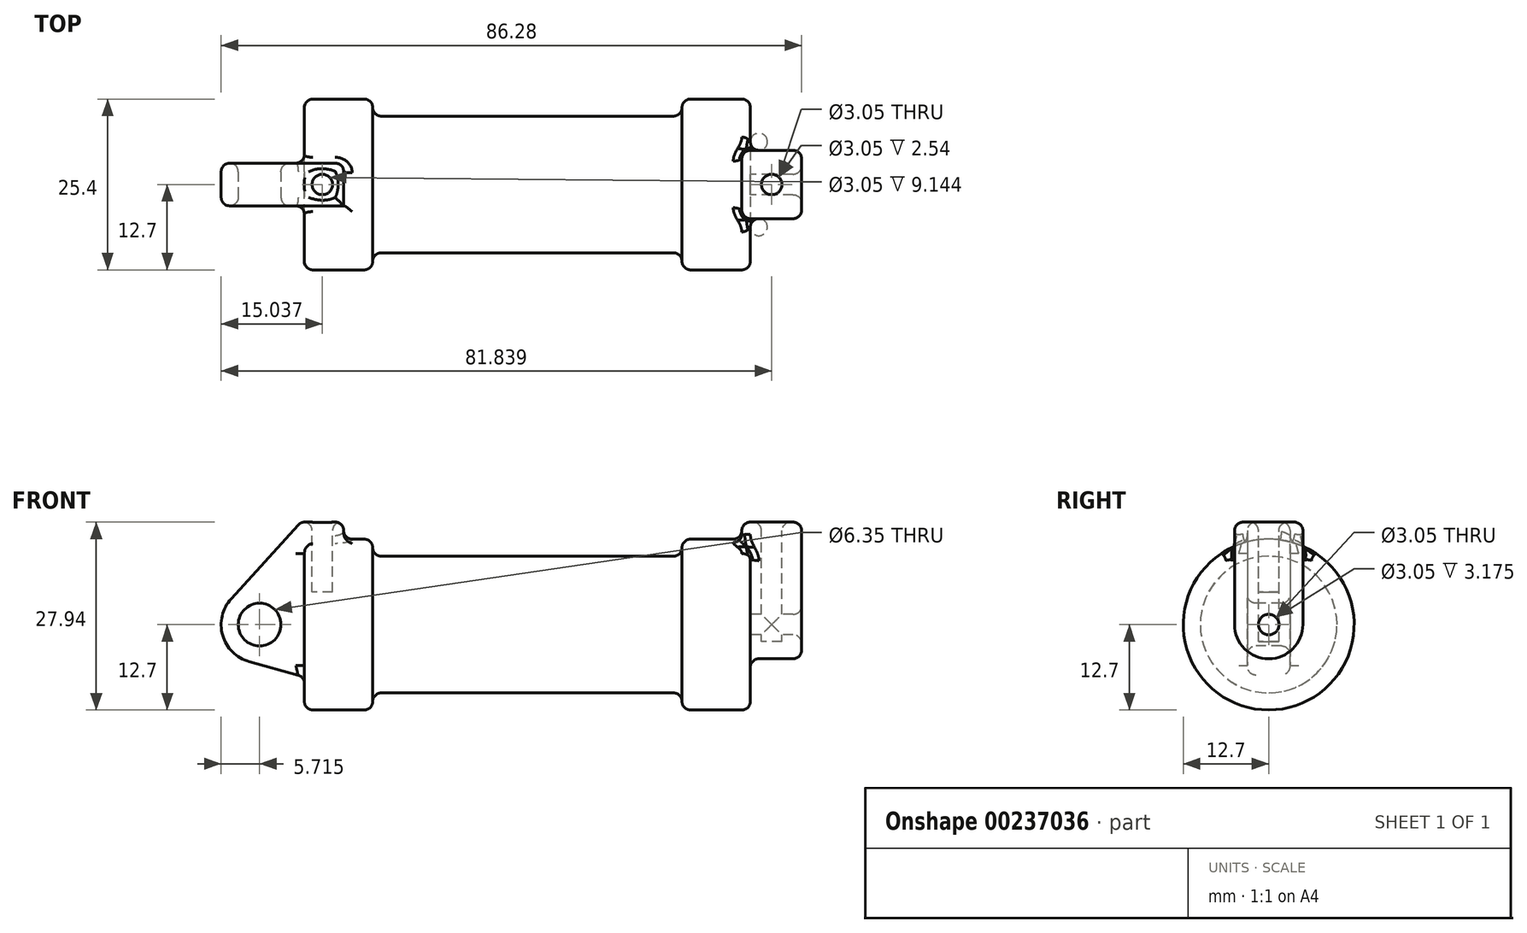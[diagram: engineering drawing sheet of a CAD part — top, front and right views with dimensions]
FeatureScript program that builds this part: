
annotation { "Feature Type Name" : "Feature", "Feature Type Description" : "" }
export const myFeature = defineFeature(function(context is Context, id is Id, definition is map)
    precondition{}
    {
        {
            var Q0;
            Q0=qCreatedBy(makeId("Front.planeOp"),FACE);
            var sketch = newSketch(context, id + "F0", { "sketchPlane" : qUnion([Q0])});
            skLineSegment(sketch, "E0", {"start": v(0, 0) * mm, "end": v(0, 12.7) * mm});
            skLineSegment(sketch, "E1", {"start": v(0, 12.7) * mm, "end": v(10.16, 12.7) * mm});
            skLineSegment(sketch, "E2", {"start": v(10.16, 12.7) * mm, "end": v(10.16, 10.16) * mm});
            skLineSegment(sketch, "E3", {"start": v(10.16, 10.16) * mm, "end": v(56.13, 10.16) * mm});
            skLineSegment(sketch, "E4", {"start": v(56.13, 10.16) * mm, "end": v(56.13, 12.7) * mm});
            skLineSegment(sketch, "E5", {"start": v(56.13, 12.7) * mm, "end": v(66.3, 12.7) * mm});
            skLineSegment(sketch, "E6", {"start": v(66.3, 12.7) * mm, "end": v(66.3, 0) * mm});
            skLineSegment(sketch, "E7", {"start": v(66.3, 0) * mm, "end": v(0, 0) * mm});
            skLineSegment(sketch, "E8", {"start": v(5.84, 15.24) * mm, "end": v(-0.5, 15.24) * mm});
            skLineSegment(sketch, "E9", {"start": v(-0.5, 15.24) * mm, "end": v(-10.88, 3.85) * mm});
            skLineSegment(sketch, "E10", {"start": v(0, 0) * mm, "end": v(-6.65, 0) * mm});
            skCircle(sketch, "E11", {"center": v(-6.65, 0) * mm, "radius": 5.72 * mm});
            skCircle(sketch, "E12", {"center": v(-6.65, 0) * mm, "radius": 3.18 * mm});
            skLineSegment(sketch, "E13", {"start": v(5.84, 15.24) * mm, "end": v(5.84, -9.4) * mm});
            skLineSegment(sketch, "E14", {"start": v(5.84, -9.4) * mm, "end": v(-8.18, -5.5) * mm});
            skSolve(sketch);
        }
        {
            var Q0;
            {var subQ0=sQuery(id+"F0.wireOp",EDGE,"E2");Q0=makeQuery(id+"F0.imprint","IMPRINT",FACE,{"disambiguationData":[TD([[makeQuery(id+"F0.imprint","IMPRINT",EDGE,{"derivedFrom":subQ0}),-1.0]])]});}
            var Q1;
            {var subQ0=sQuery(id+"F0.wireOp",EDGE,"E0");Q1=makeQuery(id+"F0.imprint","IMPRINT",FACE,{"disambiguationData":[TD([[makeQuery(id+"F0.imprint","IMPRINT",EDGE,{"derivedFrom":subQ0}),-1.0]])]});}
            var Q2;
            Q2=sQuery(id+"F0.wireOp",EDGE,"E7");
            revolve(context, id + "F1", {"entities" : qUnion([Q0, Q1]), "axis" : qUnion([Q2]), "revolveType" : RevolveType.FULL});
        }
        {
            var Q0;
            {var subQ0=sQuery(id+"F0.wireOp",EDGE,"E0");Q0=makeQuery(id+"F0.imprint","IMPRINT",FACE,{"disambiguationData":[TD([[makeQuery(id+"F0.imprint","IMPRINT",EDGE,{"derivedFrom":subQ0}),-1.0]])]});}
            var Q1;
            {var subQ3=sQuery(id+"F0.wireOp",EDGE,"E0");Q1=makeQuery(id+"F0.imprint","IMPRINT",FACE,{"disambiguationData":[TD([[makeQuery(id+"F0.imprint","IMPRINT",EDGE,{"derivedFrom":subQ3}),1.0]])]});}
            var Q2;
            {var subQ0=sQuery(id+"F0.wireOp",EDGE,"E14");Q2=makeQuery(id+"F0.imprint","IMPRINT",FACE,{"disambiguationData":[TD([[makeQuery(id+"F0.imprint","IMPRINT",EDGE,{"derivedFrom":subQ0}),-1.0]])]});}
            var Q3;
            {var subQ4=sQuery(id+"F0.wireOp",EDGE,"E12");Q3=makeQuery(id+"F0.imprint","IMPRINT",FACE,{"disambiguationData":[TD([[makeQuery(id+"F0.imprint","IMPRINT",EDGE,{"derivedFrom":subQ4}),-1.0]])]});}
            extrude(context, id + "F2", {"entities" : qUnion([Q0, Q1, Q2, Q3]), "operationType" : NewBodyOperationType.ADD, "endBound" : BoundingType.SYMMETRIC, "oppositeDirection" : true, "depth" : 6.35 * mm});
        }
        {
            var Q0;
            Q0=makeQuery(id+"F1.opRevolve","SWEPT_FACE",FACE,{"disambiguationData":[OSD([sQuery(id+"F0.wireOp",EDGE,"E6")])]});
            var sketch = newSketch(context, id + "F3", { "sketchPlane" : qUnion([Q0])});
            skCircle(sketch, "E15", {"center": v(0, 0) * mm, "radius": 1.52 * mm});
            skCircle(sketch, "E16", {"center": v(0, 0) * mm, "radius": 5.08 * mm});
            skLineSegment(sketch, "E17", {"start": v(-5.08, 0) * mm, "end": v(-5.08, 15.24) * mm});
            skLineSegment(sketch, "E18", {"start": v(-5.08, 15.24) * mm, "end": v(5.08, 15.24) * mm});
            skLineSegment(sketch, "E19", {"start": v(5.08, 15.24) * mm, "end": v(5.08, 0) * mm});
            skSolve(sketch);
        }
        {
            var Q0;
            Q0 = qSketchRegion(id + "F3", true);
            extrude(context, id + "F4", {"entities" : qUnion([Q0]), "operationType" : NewBodyOperationType.ADD, "depth" : 7.62 * mm, "hasSecondDirection" : true, "secondDirectionOppositeDirection" : true, "secondDirectionDepth" : 1.27 * mm});
        }
        {
            var Q0;
            Q0=makeQuery(id+"F4.opExtrude","SWEPT_FACE",FACE,{"disambiguationData":[OSD([sQuery(id+"F3.wireOp",EDGE,"E18")])]});
            var sketch = newSketch(context, id + "F5", { "sketchPlane" : qUnion([Q0])});
            skCircle(sketch, "E20", {"center": v(69.47, 0) * mm, "radius": 1.52 * mm});
            skSolve(sketch);
        }
        {
            var Q0;
            Q0=makeQuery(id+"F2.opExtrude","SWEPT_FACE",FACE,{"disambiguationData":[OSD([sQuery(id+"F0.wireOp",EDGE,"E8")])]});
            var sketch = newSketch(context, id + "F6", { "sketchPlane" : qUnion([Q0])});
            skCircle(sketch, "E21", {"center": v(2.67, 0) * mm, "radius": 1.52 * mm});
            skSolve(sketch);
        }
        {
            var Q0;
            Q0 = qSketchRegion(id + "F5", true);
            extrude(context, id + "F7", {"entities" : qUnion([Q0]), "operationType" : NewBodyOperationType.REMOVE, "oppositeDirection" : true, "depth" : 17.78 * mm});
        }
        {
            var Q0;
            Q0 = qSketchRegion(id + "F6", true);
            extrude(context, id + "F8", {"entities" : qUnion([Q0]), "operationType" : NewBodyOperationType.REMOVE, "oppositeDirection" : true, "depth" : 10.4 * mm});
        }
        {
            var Q0;
            Q0=makeQuery(id+"F1.opRevolve","SWEPT_FACE",FACE,{"disambiguationData":[OSD([sQuery(id+"F0.wireOp",EDGE,"E5")])]});
            var Q1;
            Q1=makeQuery(id+"F1.opRevolve","SWEPT_FACE",FACE,{"disambiguationData":[OSD([sQuery(id+"F0.wireOp",EDGE,"E3")])]});
            var Q2;
            Q2=makeQuery(id+"F4.opExtrude","SWEPT_FACE",FACE,{"disambiguationData":[OSD([sQuery(id+"F3.wireOp",EDGE,"E19")])]});
            var Q3;
            Q3=makeQuery(id+"F4.opExtrude","CAP_FACE",FACE,{"disambiguationData":[OSD([sQuery(id+"F3.wireOp",EDGE,"E15"),sQuery(id+"F3.wireOp",EDGE,"E16"),sQuery(id+"F3.wireOp",EDGE,"E17"),sQuery(id+"F3.wireOp",EDGE,"E18"),sQuery(id+"F3.wireOp",EDGE,"E19")])],"isStart":true});
            var Q4;
            Q4=makeQuery(id+"F4.opExtrude","SWEPT_FACE",FACE,{"disambiguationData":[OSD([sQuery(id+"F3.wireOp",EDGE,"E18")])]});
            var Q5;
            Q5=makeQuery(id+"F1.opRevolve","SWEPT_EDGE",EDGE,{"disambiguationData":[OSD([sQuery(id+"F0.wireOp",EDGE,"E4"),sQuery(id+"F0.wireOp",EDGE,"E5")])]});
            var Q6;
            Q6=makeQuery(id+"F1.opRevolve","SWEPT_EDGE",EDGE,{"disambiguationData":[OSD([sQuery(id+"F0.wireOp",EDGE,"E0"),sQuery(id+"F0.wireOp",EDGE,"E1")])]});
            var Q7;
            Q7=makeQuery(id+"F1.opRevolve","SWEPT_FACE",FACE,{"disambiguationData":[OSD([sQuery(id+"F0.wireOp",EDGE,"E1")])]});
            var Q8;
            Q8=makeQuery(id+"F2.opExtrude","CAP_FACE",FACE,{"disambiguationData":[OSD([sQuery(id+"F0.wireOp",EDGE,"E8"),sQuery(id+"F0.wireOp",EDGE,"E9"),sQuery(id+"F0.wireOp",EDGE,"E11"),sQuery(id+"F0.wireOp",EDGE,"E12"),sQuery(id+"F0.wireOp",EDGE,"E13"),sQuery(id+"F0.wireOp",EDGE,"E14")])],"isStart":false});
            var Q9;
            Q9=makeQuery(id+"F2.opExtrude","SWEPT_FACE",FACE,{"disambiguationData":[OSD([sQuery(id+"F0.wireOp",EDGE,"E9")])]});
            var Q10;
            Q10=makeQuery(id+"F2.opExtrude","SWEPT_FACE",FACE,{"disambiguationData":[OSD([sQuery(id+"F0.wireOp",EDGE,"E11")])]});
            var Q11;
            Q11=makeQuery(id+"F2.opExtrude","SWEPT_FACE",FACE,{"disambiguationData":[OSD([sQuery(id+"F0.wireOp",EDGE,"E8")])]});
            var Q12;
            Q12=makeQuery(id+"F4.opExtrude","CAP_FACE",FACE,{"disambiguationData":[OSD([sQuery(id+"F3.wireOp",EDGE,"E15"),sQuery(id+"F3.wireOp",EDGE,"E16"),sQuery(id+"F3.wireOp",EDGE,"E17"),sQuery(id+"F3.wireOp",EDGE,"E18"),sQuery(id+"F3.wireOp",EDGE,"E19")])],"isStart":false});
            var Q13;
            Q13=makeQuery(id+"F2.opExtrude","SWEPT_FACE",FACE,{"disambiguationData":[OSD([sQuery(id+"F0.wireOp",EDGE,"E12")])]});
            var Q14;
            Q14=makeQuery(id+"F1.opRevolve","SWEPT_FACE",FACE,{"disambiguationData":[OSD([sQuery(id+"F0.wireOp",EDGE,"E0")])]});
            fillet(context, id + "F9", {"entities" : qUnion([Q0, Q1, Q2, Q3, Q4, Q5, Q6, Q7, Q8, Q9, Q10, Q11, Q12, Q13, Q14]), "radius" : 1.27 * mm, "tangentPropagation" : true, "allowEdgeOverflow" : false});
        }
    });
